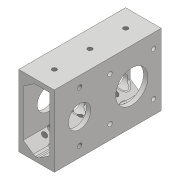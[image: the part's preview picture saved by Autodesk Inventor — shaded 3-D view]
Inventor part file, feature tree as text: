
AUTODESK INVENTOR PART (.ipt)
format: ipt  version: 2018 (Build 220112000, 112)  size: 627,712 bytes
history: native  units: mm
features: sketch x7, hole x5, extrude x3, chamfer x3, fillet x3, other x3, shell x1, reference x1, projected_geometry x1
ambient origin geometry x8: Origin, YZ Plane, XZ Plane, XY Plane, X Axis, Y Axis, Z Axis, Center Point
bodies: Solid1 (feature_tree)
feature tree (27):
  extrude  "Extrusion1"  Depth=25.4mm
  shell  "Shell1"  Thickness=76.2mm
  chamfer  "Chamfer1"  Distance=23.0mm
  chamfer  "Chamfer2"  Distance=50.8mm
  chamfer  "Chamfer3"  Distance=16.0mm
  sketch  "Sketch2"  dims[d4=3.175mm]
  hole  "Hole1"  [1 undecoded]
  hole  "Hole2"  [1 undecoded]
  extrude  "Extrusion2"  Depth=10.0mm
  extrude  "Extrusion3"  Depth=10.0mm
  hole  "Hole4"  [1 undecoded]
  hole  "Hole5"  [1 undecoded]
  fillet  "Fillet1"  Radius=8.0mm
  fillet  "Fillet2"  Radius=3.0mm
  fillet  "Fillet3"  Radius=3.0mm
  hole  "Hole7"  [1 undecoded]
  sketch  "Sketch1"  dims[d0=50.8mm d1=25.4mm d2=76.2mm d3=0.0mm]
  sketch  "Sketch3"  dims[d5=31.0mm]
  sketch  "Sketch4"  dims[d6=31.0mm]
  sketch  "Sketch6"  dims[d7=21.0mm]
  sketch  "Sketch7"  dims[d8=3.2mm d9=6.0mm d10=8.0mm d11=22.225mm d12=90.0deg d13=8.0mm d14=20.594885mm]
  reference  "Reference1"
  sketch  "Sketch10"  dims[d15=10.0mm d16=6.0mm d17=6.5mm d18=3.0mm d19=90.0deg d20=8.0mm d21=20.594885mm d22=23.0mm d23=50.8mm d24=0.0mm d25=16.0mm d26=18.0mm d27=50.8mm d28=0.0mm d40=3.242mm d41=100.0mm d42=6.5mm d43=3.0mm d44=90.0deg d45=11.8mm d46=20.594885mm d47=36.0mm d48=3.242mm d49=100.0mm d50=6.5mm d51=3.0mm d52=90.0deg d53=11.8mm d54=20.594885mm d55=50.8mm d56=8.0mm d57=5.5mm d58=45.0deg d59=5.5mm d60=8.0mm d61=45.0deg d62=8.0mm d63=5.5mm d64=45.0deg d68=3.0mm d69=3.0mm d70=1.5mm d86=14.0mm d87=3.242mm d88=8.0mm d89=4.0mm d90=2.0mm d91=90.0deg d92=11.8mm d93=20.594885mm]
  projected_geometry  "Projected Loop2"
  parser-record x1  (decoder bookkeeping rows leaked as tree rows — omitted from the tree; the rows remain in map.json)
  other  "AMR_Transm2.iam"
  other  "7804K147_STAINLESS STEEL BALL BEARING:2"
note: 5 required parameter values undecoded (feature->parameter linkage not recoverable at this tier; creation-order binding heuristic only, values carry confidence <= 0.55)
note: 1 file-system path scrubbed to <path> (originals preserved in map.json)
